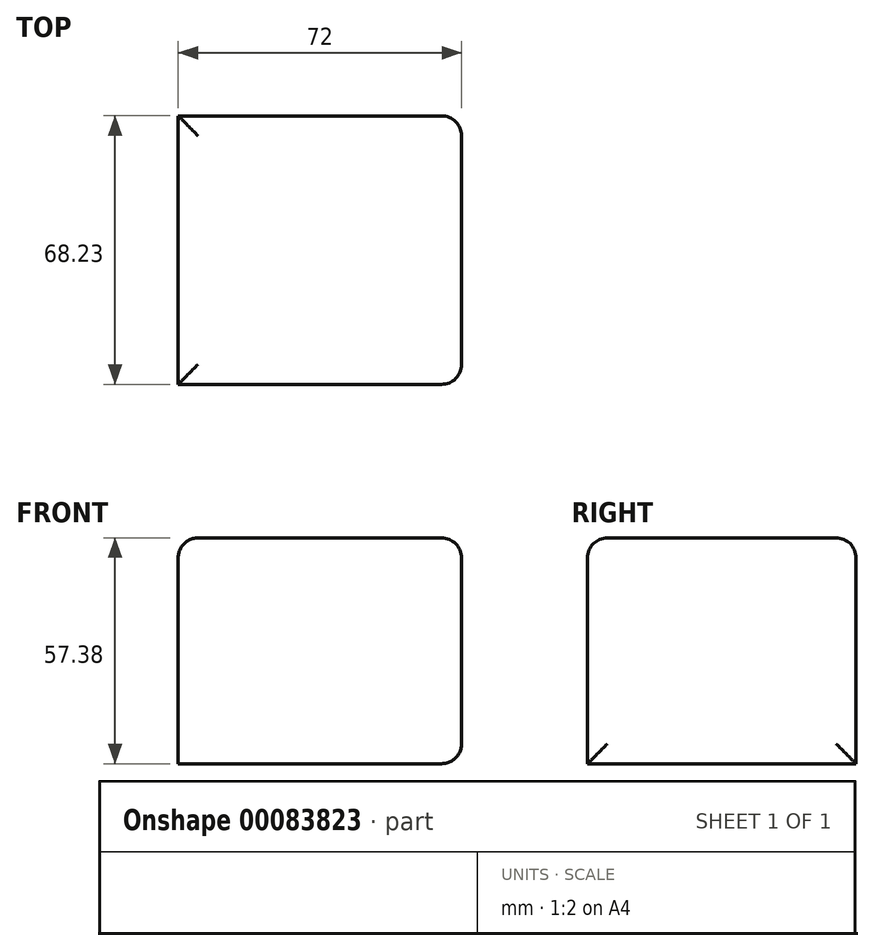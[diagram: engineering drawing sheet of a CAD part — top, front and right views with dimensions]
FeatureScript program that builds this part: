
annotation { "Feature Type Name" : "Feature", "Feature Type Description" : "" }
export const myFeature = defineFeature(function(context is Context, id is Id, definition is map)
    precondition{}
    {
        {
            var Q0;
            Q0=qCreatedBy(makeId("Top.planeOp"),FACE);
            var sketch = newSketch(context, id + "F0", { "sketchPlane" : qUnion([Q0])});
            skLineSegment(sketch, "E0.bottom", {"start": v(-22.27, -25.12) * mm, "end": v(49.73, -25.12) * mm});
            skLineSegment(sketch, "E0.top", {"start": v(-22.27, 43.1) * mm, "end": v(49.73, 43.1) * mm});
            skLineSegment(sketch, "E0.left", {"start": v(-22.27, -25.12) * mm, "end": v(-22.27, 43.1) * mm});
            skLineSegment(sketch, "E0.right", {"start": v(49.73, -25.12) * mm, "end": v(49.73, 43.1) * mm});
            skSolve(sketch);
        }
        {
            var Q0;
            Q0 = qSketchRegion(id + "F0", true);
            extrude(context, id + "F1", {"entities" : qUnion([Q0]), "depth" : 57.38 * mm});
        }
        {
            var Q0;
            Q0=makeQuery(id+"F1.opExtrude","CAP_FACE",FACE,{"disambiguationData":[OSD([sQuery(id+"F0.wireOp",EDGE,"E0.bottom"),sQuery(id+"F0.wireOp",EDGE,"E0.top"),sQuery(id+"F0.wireOp",EDGE,"E0.left"),sQuery(id+"F0.wireOp",EDGE,"E0.right")])],"isStart":false});
            var Q1;
            Q1=makeQuery(id+"F1.opExtrude","SWEPT_FACE",FACE,{"disambiguationData":[OSD([sQuery(id+"F0.wireOp",EDGE,"E0.right")])]});
            fillet(context, id + "F2", {"entities" : qUnion([Q0, Q1]), "radius" : 5.08 * mm, "tangentPropagation" : true, "allowEdgeOverflow" : false});
        }
    });
